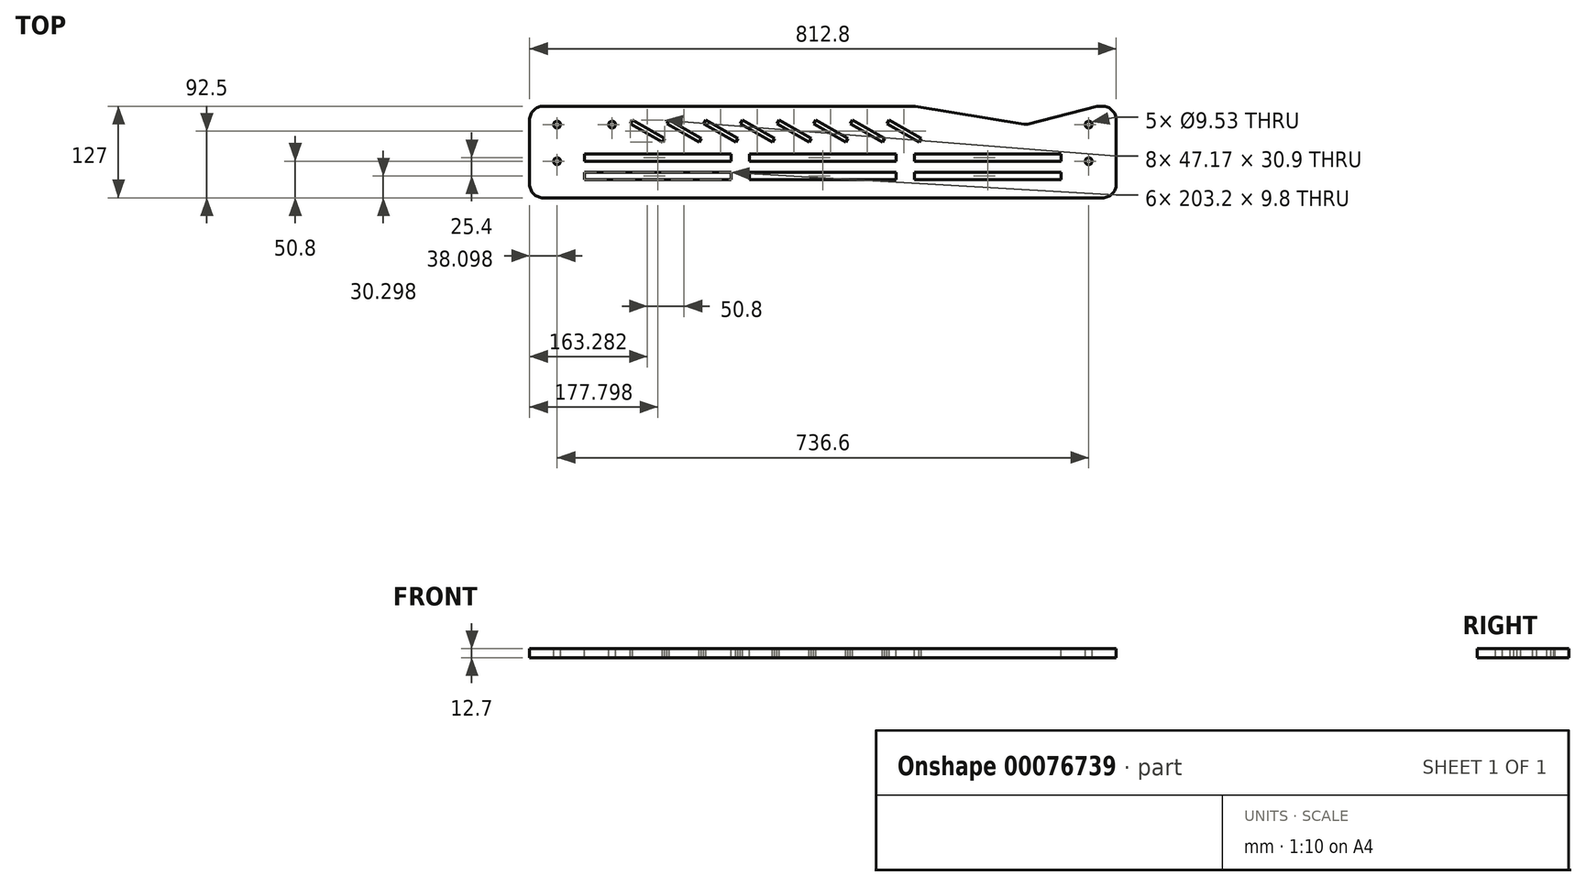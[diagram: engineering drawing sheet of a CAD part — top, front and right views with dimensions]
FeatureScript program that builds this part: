
annotation { "Feature Type Name" : "Feature", "Feature Type Description" : "" }
export const myFeature = defineFeature(function(context is Context, id is Id, definition is map)
    precondition{}
    {
        {
            var Q0;
            Q0=qCreatedBy(makeId("Top.planeOp"),FACE);
            var sketch = newSketch(context, id + "F0", { "sketchPlane" : qUnion([Q0])});
            skLineSegment(sketch, "E0.bottom", {"start": v(-305.25, 25.4) * mm, "end": v(208.06, 25.4) * mm});
            skLineSegment(sketch, "E0.top", {"start": v(-305.25, -101.6) * mm, "end": v(469.45, -101.6) * mm});
            skLineSegment(sketch, "E0.left", {"start": v(-324.3, 6.35) * mm, "end": v(-324.3, -82.55) * mm});
            skLineSegment(sketch, "E0.right", {"start": v(488.5, 6.35) * mm, "end": v(488.5, -82.55) * mm});
            skPoint(sketch, "E1.visualSharp", {"position": v(-324.3, 25.4) * mm});
            skArc(sketch, "E1.filletArc", {"start": v(-305.25, 25.4) * mm, "mid": v(-318.72, 19.82) * mm, "end": v(-324.3, 6.35) * mm});
            skPoint(sketch, "E2.visualSharp", {"position": v(-324.3, -101.6) * mm});
            skArc(sketch, "E2.filletArc", {"start": v(-324.3, -82.55) * mm, "mid": v(-318.72, -96.02) * mm, "end": v(-305.25, -101.6) * mm});
            skPoint(sketch, "E3.visualSharp", {"position": v(488.5, -101.6) * mm});
            skArc(sketch, "E3.filletArc", {"start": v(469.45, -101.6) * mm, "mid": v(482.92, -96.02) * mm, "end": v(488.5, -82.55) * mm});
            skPoint(sketch, "E4.visualSharp", {"position": v(488.5, 25.4) * mm});
            skArc(sketch, "E4.filletArc", {"start": v(488.5, 6.35) * mm, "mid": v(482.92, 19.82) * mm, "end": v(469.45, 25.4) * mm});
            skLineSegment(sketch, "E5.trimOffspring", {"start": v(464.68, 25.4) * mm, "end": v(469.45, 25.4) * mm});
            skLineSegment(sketch, "E6", {"start": v(461.56, 25) * mm, "end": v(365.62, 0.65) * mm});
            skLineSegment(sketch, "E7", {"start": v(360.43, 0.43) * mm, "end": v(210.12, 25.23) * mm});
            skPoint(sketch, "E8.visualSharp", {"position": v(363.04, 0) * mm});
            skArc(sketch, "E8.filletArc", {"start": v(360.43, 0.43) * mm, "mid": v(363.03, 0.27) * mm, "end": v(365.62, 0.65) * mm});
            skPoint(sketch, "E9.visualSharp", {"position": v(209.1, 25.4) * mm});
            skArc(sketch, "E9.filletArc", {"start": v(210.12, 25.23) * mm, "mid": v(209.1, 25.36) * mm, "end": v(208.06, 25.4) * mm});
            skPoint(sketch, "E10.visualSharp", {"position": v(463.1, 25.4) * mm});
            skArc(sketch, "E10.filletArc", {"start": v(464.68, 25.4) * mm, "mid": v(463.1, 25.3) * mm, "end": v(461.56, 25) * mm});
            skSolve(sketch);
        }
        {
            var Q0;
            Q0=makeQuery(id+"F0.imprint","IMPRINT",FACE,{"disambiguationData":[TD([[makeQuery(id+"F0.imprint","IMPRINT",EDGE,{"derivedFrom":sQuery(id+"F0.wireOp",EDGE,"E0.bottom")}),-1.0]])]});
            extrude(context, id + "F1", {"entities" : qUnion([Q0]), "depth" : 12.7 * mm});
        }
        {
            var Q0;
            Q0=makeQuery(id+"F1.opExtrude","CAP_FACE",FACE,{"disambiguationData":[OSD([sQuery(id+"F0.wireOp",EDGE,"E0.bottom"),sQuery(id+"F0.wireOp",EDGE,"E0.top"),sQuery(id+"F0.wireOp",EDGE,"E0.left"),sQuery(id+"F0.wireOp",EDGE,"E0.right"),sQuery(id+"F0.wireOp",EDGE,"965c0fb1-0d6b-43e8-9724-7c81c577700a"),sQuery(id+"F0.wireOp",EDGE,"E1.filletArc"),sQuery(id+"F0.wireOp",EDGE,"E2.filletArc"),sQuery(id+"F0.wireOp",EDGE,"E3.filletArc"),sQuery(id+"F0.wireOp",EDGE,"E4.filletArc"),sQuery(id+"F0.wireOp",EDGE,"E5.trimOffspring")])],"isStart":false});
            var sketch = newSketch(context, id + "F2", { "sketchPlane" : qUnion([Q0])});
            skCircle(sketch, "E11", {"center": v(-286.2, 0) * mm, "radius": 4.76 * mm});
            skCircle(sketch, "E12", {"center": v(-286.2, -50.8) * mm, "radius": 4.76 * mm});
            skCircle(sketch, "E13", {"center": v(450.4, 0) * mm, "radius": 4.76 * mm});
            skCircle(sketch, "E14", {"center": v(450.4, -50.8) * mm, "radius": 4.76 * mm});
            skCircle(sketch, "E15", {"center": v(-210, 0) * mm, "radius": 4.76 * mm});
            skSolve(sketch);
        }
        {
            var Q0;
            Q0=makeQuery(id+"F2.imprint","IMPRINT",FACE,{"disambiguationData":[TD([[makeQuery(id+"F2.imprint","IMPRINT",EDGE,{"derivedFrom":sQuery(id+"F2.wireOp",EDGE,"E11")}),1.0]])]});
            var Q1;
            Q1=makeQuery(id+"F2.imprint","IMPRINT",FACE,{"disambiguationData":[TD([[makeQuery(id+"F2.imprint","IMPRINT",EDGE,{"derivedFrom":sQuery(id+"F2.wireOp",EDGE,"E12")}),1.0]])]});
            var Q2;
            Q2=makeQuery(id+"F2.imprint","IMPRINT",FACE,{"disambiguationData":[TD([[makeQuery(id+"F2.imprint","IMPRINT",EDGE,{"derivedFrom":sQuery(id+"F2.wireOp",EDGE,"E15")}),1.0]])]});
            var Q3;
            Q3=makeQuery(id+"F2.imprint","IMPRINT",FACE,{"disambiguationData":[TD([[makeQuery(id+"F2.imprint","IMPRINT",EDGE,{"derivedFrom":sQuery(id+"F2.wireOp",EDGE,"E13")}),1.0]])]});
            var Q4;
            Q4=makeQuery(id+"F2.imprint","IMPRINT",FACE,{"disambiguationData":[TD([[makeQuery(id+"F2.imprint","IMPRINT",EDGE,{"derivedFrom":sQuery(id+"F2.wireOp",EDGE,"E14")}),1.0]])]});
            extrude(context, id + "F3", {"entities" : qUnion([Q0, Q1, Q2, Q3, Q4]), "operationType" : NewBodyOperationType.REMOVE, "endBound" : BoundingType.THROUGH_ALL, "oppositeDirection" : true, "depth" : 25.4 * mm});
        }
        {
            var Q0;
            Q0=makeQuery(id+"F1.opExtrude","CAP_FACE",FACE,{"disambiguationData":[OSD([sQuery(id+"F0.wireOp",EDGE,"E0.bottom"),sQuery(id+"F0.wireOp",EDGE,"E0.top"),sQuery(id+"F0.wireOp",EDGE,"E0.left"),sQuery(id+"F0.wireOp",EDGE,"E0.right"),sQuery(id+"F0.wireOp",EDGE,"965c0fb1-0d6b-43e8-9724-7c81c577700a"),sQuery(id+"F0.wireOp",EDGE,"E1.filletArc"),sQuery(id+"F0.wireOp",EDGE,"E2.filletArc"),sQuery(id+"F0.wireOp",EDGE,"E3.filletArc"),sQuery(id+"F0.wireOp",EDGE,"E4.filletArc"),sQuery(id+"F0.wireOp",EDGE,"E5.trimOffspring")])],"isStart":false});
            var sketch = newSketch(context, id + "F4", { "sketchPlane" : qUnion([Q0])});
            skLineSegment(sketch, "E16.bottom", {"start": v(412.3, -76.2) * mm, "end": v(209.1, -76.2) * mm});
            skLineSegment(sketch, "E16.top", {"start": v(412.3, -66.4) * mm, "end": v(209.1, -66.4) * mm});
            skLineSegment(sketch, "E16.left", {"start": v(412.3, -76.2) * mm, "end": v(412.3, -66.4) * mm});
            skLineSegment(sketch, "E16.right", {"start": v(209.1, -76.2) * mm, "end": v(209.1, -66.4) * mm});
            skLineSegment(sketch, "E17.0.1.0", {"start": v(412.3, -41) * mm, "end": v(209.1, -41) * mm});
            skLineSegment(sketch, "E17.0.1.1", {"start": v(412.3, -50.8) * mm, "end": v(412.3, -41) * mm});
            skLineSegment(sketch, "E17.0.1.2", {"start": v(412.3, -50.8) * mm, "end": v(209.1, -50.8) * mm});
            skLineSegment(sketch, "E17.0.1.3", {"start": v(209.1, -50.8) * mm, "end": v(209.1, -41) * mm});
            skLineSegment(sketch, "E17.1.0.0", {"start": v(183.7, -66.4) * mm, "end": v(-19.5, -66.4) * mm});
            skLineSegment(sketch, "E17.1.0.1", {"start": v(183.7, -76.2) * mm, "end": v(183.7, -66.4) * mm});
            skLineSegment(sketch, "E17.1.0.2", {"start": v(183.7, -76.2) * mm, "end": v(-19.5, -76.2) * mm});
            skLineSegment(sketch, "E17.1.0.3", {"start": v(-19.5, -76.2) * mm, "end": v(-19.5, -66.4) * mm});
            skLineSegment(sketch, "E17.1.1.0", {"start": v(183.7, -41) * mm, "end": v(-19.5, -41) * mm});
            skLineSegment(sketch, "E17.1.1.1", {"start": v(183.7, -50.8) * mm, "end": v(183.7, -41) * mm});
            skLineSegment(sketch, "E17.1.1.2", {"start": v(183.7, -50.8) * mm, "end": v(-19.5, -50.8) * mm});
            skLineSegment(sketch, "E17.1.1.3", {"start": v(-19.5, -50.8) * mm, "end": v(-19.5, -41) * mm});
            skLineSegment(sketch, "E17.2.0.0", {"start": v(-44.9, -66.4) * mm, "end": v(-248.1, -66.4) * mm});
            skLineSegment(sketch, "E17.2.0.1", {"start": v(-44.9, -76.2) * mm, "end": v(-44.9, -66.4) * mm});
            skLineSegment(sketch, "E17.2.0.2", {"start": v(-44.9, -76.2) * mm, "end": v(-248.1, -76.2) * mm});
            skLineSegment(sketch, "E17.2.0.3", {"start": v(-248.1, -76.2) * mm, "end": v(-248.1, -66.4) * mm});
            skLineSegment(sketch, "E17.2.1.0", {"start": v(-44.9, -41) * mm, "end": v(-248.1, -41) * mm});
            skLineSegment(sketch, "E17.2.1.1", {"start": v(-44.9, -50.8) * mm, "end": v(-44.9, -41) * mm});
            skLineSegment(sketch, "E17.2.1.2", {"start": v(-44.9, -50.8) * mm, "end": v(-248.1, -50.8) * mm});
            skLineSegment(sketch, "E17.2.1.3", {"start": v(-248.1, -50.8) * mm, "end": v(-248.1, -41) * mm});
            skLineSegment(sketch, "E17.direction1", {"start": v(209.1, -76.2) * mm, "end": v(-19.5, -76.2) * mm, "construction": true});
            skLineSegment(sketch, "E17.direction2", {"start": v(209.1, -76.2) * mm, "end": v(209.1, -50.8) * mm, "construction": true});
            skSolve(sketch);
        }
        {
            var Q0;
            Q0=makeQuery(id+"F4.imprint","IMPRINT",FACE,{"disambiguationData":[TD([[makeQuery(id+"F4.imprint","IMPRINT",EDGE,{"derivedFrom":sQuery(id+"F4.wireOp",EDGE,"E16.bottom")}),-1.0]])]});
            var Q1;
            Q1=makeQuery(id+"F4.imprint","IMPRINT",FACE,{"disambiguationData":[TD([[makeQuery(id+"F4.imprint","IMPRINT",EDGE,{"derivedFrom":sQuery(id+"F4.wireOp",EDGE,"E17.0.1.0")}),1.0]])]});
            var Q2;
            Q2=makeQuery(id+"F4.imprint","IMPRINT",FACE,{"disambiguationData":[TD([[makeQuery(id+"F4.imprint","IMPRINT",EDGE,{"derivedFrom":sQuery(id+"F4.wireOp",EDGE,"E17.1.1.0")}),1.0]])]});
            var Q3;
            Q3=makeQuery(id+"F4.imprint","IMPRINT",FACE,{"disambiguationData":[TD([[makeQuery(id+"F4.imprint","IMPRINT",EDGE,{"derivedFrom":sQuery(id+"F4.wireOp",EDGE,"E17.1.0.0")}),1.0]])]});
            var Q4;
            Q4=makeQuery(id+"F4.imprint","IMPRINT",FACE,{"disambiguationData":[TD([[makeQuery(id+"F4.imprint","IMPRINT",EDGE,{"derivedFrom":sQuery(id+"F4.wireOp",EDGE,"E17.2.0.0")}),1.0]])]});
            var Q5;
            Q5=makeQuery(id+"F4.imprint","IMPRINT",FACE,{"disambiguationData":[TD([[makeQuery(id+"F4.imprint","IMPRINT",EDGE,{"derivedFrom":sQuery(id+"F4.wireOp",EDGE,"E17.2.1.0")}),1.0]])]});
            extrude(context, id + "F5", {"entities" : qUnion([Q0, Q1, Q2, Q3, Q4, Q5]), "operationType" : NewBodyOperationType.REMOVE, "endBound" : BoundingType.THROUGH_ALL, "oppositeDirection" : true, "depth" : 25.4 * mm});
        }
        {
            var Q0;
            Q0=makeQuery(id+"F1.opExtrude","CAP_FACE",FACE,{"disambiguationData":[OSD([sQuery(id+"F0.wireOp",EDGE,"E0.bottom"),sQuery(id+"F0.wireOp",EDGE,"E0.top"),sQuery(id+"F0.wireOp",EDGE,"E0.left"),sQuery(id+"F0.wireOp",EDGE,"E0.right"),sQuery(id+"F0.wireOp",EDGE,"965c0fb1-0d6b-43e8-9724-7c81c577700a"),sQuery(id+"F0.wireOp",EDGE,"E1.filletArc"),sQuery(id+"F0.wireOp",EDGE,"E2.filletArc"),sQuery(id+"F0.wireOp",EDGE,"E3.filletArc"),sQuery(id+"F0.wireOp",EDGE,"E4.filletArc"),sQuery(id+"F0.wireOp",EDGE,"E5.trimOffspring")])],"isStart":false});
            var sketch = newSketch(context, id + "F6", { "sketchPlane" : qUnion([Q0])});
            skLineSegment(sketch, "E18.bottom", {"start": v(-181.43, 6.35) * mm, "end": v(-137.43, -19.05) * mm});
            skLineSegment(sketch, "E18.top", {"start": v(-184.6, 0.85) * mm, "end": v(-140.6, -24.55) * mm});
            skLineSegment(sketch, "E18.left", {"start": v(-181.43, 6.35) * mm, "end": v(-184.6, 0.85) * mm});
            skLineSegment(sketch, "E18.right", {"start": v(-137.43, -19.05) * mm, "end": v(-140.6, -24.55) * mm});
            skLineSegment(sketch, "E19.1.0.0", {"start": v(-130.63, 6.35) * mm, "end": v(-86.63, -19.05) * mm});
            skLineSegment(sketch, "E19.1.0.1", {"start": v(-133.8, 0.85) * mm, "end": v(-89.8, -24.55) * mm});
            skLineSegment(sketch, "E19.1.0.2", {"start": v(-130.63, 6.35) * mm, "end": v(-133.8, 0.85) * mm});
            skLineSegment(sketch, "E19.1.0.3", {"start": v(-86.63, -19.05) * mm, "end": v(-89.8, -24.55) * mm});
            skLineSegment(sketch, "E19.2.0.0", {"start": v(-79.83, 6.35) * mm, "end": v(-35.83, -19.05) * mm});
            skLineSegment(sketch, "E19.2.0.1", {"start": v(-83, 0.85) * mm, "end": v(-39, -24.55) * mm});
            skLineSegment(sketch, "E19.2.0.2", {"start": v(-79.83, 6.35) * mm, "end": v(-83, 0.85) * mm});
            skLineSegment(sketch, "E19.2.0.3", {"start": v(-35.83, -19.05) * mm, "end": v(-39, -24.55) * mm});
            skLineSegment(sketch, "E19.3.0.0", {"start": v(-29.03, 6.35) * mm, "end": v(14.97, -19.05) * mm});
            skLineSegment(sketch, "E19.3.0.1", {"start": v(-32.2, 0.85) * mm, "end": v(11.8, -24.55) * mm});
            skLineSegment(sketch, "E19.3.0.2", {"start": v(-29.03, 6.35) * mm, "end": v(-32.2, 0.85) * mm});
            skLineSegment(sketch, "E19.3.0.3", {"start": v(14.97, -19.05) * mm, "end": v(11.8, -24.55) * mm});
            skLineSegment(sketch, "E19.4.0.0", {"start": v(21.77, 6.35) * mm, "end": v(65.77, -19.05) * mm});
            skLineSegment(sketch, "E19.4.0.1", {"start": v(18.6, 0.85) * mm, "end": v(62.6, -24.55) * mm});
            skLineSegment(sketch, "E19.4.0.2", {"start": v(21.77, 6.35) * mm, "end": v(18.6, 0.85) * mm});
            skLineSegment(sketch, "E19.4.0.3", {"start": v(65.77, -19.05) * mm, "end": v(62.6, -24.55) * mm});
            skLineSegment(sketch, "E19.5.0.0", {"start": v(72.57, 6.35) * mm, "end": v(116.57, -19.05) * mm});
            skLineSegment(sketch, "E19.5.0.1", {"start": v(69.4, 0.85) * mm, "end": v(113.4, -24.55) * mm});
            skLineSegment(sketch, "E19.5.0.2", {"start": v(72.57, 6.35) * mm, "end": v(69.4, 0.85) * mm});
            skLineSegment(sketch, "E19.5.0.3", {"start": v(116.57, -19.05) * mm, "end": v(113.4, -24.55) * mm});
            skLineSegment(sketch, "E19.6.0.0", {"start": v(123.37, 6.35) * mm, "end": v(167.37, -19.05) * mm});
            skLineSegment(sketch, "E19.6.0.1", {"start": v(120.2, 0.85) * mm, "end": v(164.2, -24.55) * mm});
            skLineSegment(sketch, "E19.6.0.2", {"start": v(123.37, 6.35) * mm, "end": v(120.2, 0.85) * mm});
            skLineSegment(sketch, "E19.6.0.3", {"start": v(167.37, -19.05) * mm, "end": v(164.2, -24.55) * mm});
            skLineSegment(sketch, "E19.7.0.0", {"start": v(174.17, 6.35) * mm, "end": v(218.17, -19.05) * mm});
            skLineSegment(sketch, "E19.7.0.1", {"start": v(171, 0.85) * mm, "end": v(215, -24.55) * mm});
            skLineSegment(sketch, "E19.7.0.2", {"start": v(174.17, 6.35) * mm, "end": v(171, 0.85) * mm});
            skLineSegment(sketch, "E19.7.0.3", {"start": v(218.17, -19.05) * mm, "end": v(215, -24.55) * mm});
            skLineSegment(sketch, "E19.direction1", {"start": v(-184.6, 0.85) * mm, "end": v(-133.8, 0.85) * mm, "construction": true});
            skSolve(sketch);
        }
        {
            var Q0;
            Q0=makeQuery(id+"F6.imprint","IMPRINT",FACE,{"disambiguationData":[TD([[makeQuery(id+"F6.imprint","IMPRINT",EDGE,{"derivedFrom":sQuery(id+"F6.wireOp",EDGE,"E18.bottom")}),-1.0]])]});
            var Q1;
            Q1=makeQuery(id+"F6.imprint","IMPRINT",FACE,{"disambiguationData":[TD([[makeQuery(id+"F6.imprint","IMPRINT",EDGE,{"derivedFrom":sQuery(id+"F6.wireOp",EDGE,"E19.1.0.0")}),-1.0]])]});
            var Q2;
            Q2=makeQuery(id+"F6.imprint","IMPRINT",FACE,{"disambiguationData":[TD([[makeQuery(id+"F6.imprint","IMPRINT",EDGE,{"derivedFrom":sQuery(id+"F6.wireOp",EDGE,"E19.2.0.0")}),-1.0]])]});
            var Q3;
            Q3=makeQuery(id+"F6.imprint","IMPRINT",FACE,{"disambiguationData":[TD([[makeQuery(id+"F6.imprint","IMPRINT",EDGE,{"derivedFrom":sQuery(id+"F6.wireOp",EDGE,"E19.3.0.0")}),-1.0]])]});
            var Q4;
            Q4=makeQuery(id+"F6.imprint","IMPRINT",FACE,{"disambiguationData":[TD([[makeQuery(id+"F6.imprint","IMPRINT",EDGE,{"derivedFrom":sQuery(id+"F6.wireOp",EDGE,"E19.4.0.0")}),-1.0]])]});
            var Q5;
            Q5=makeQuery(id+"F6.imprint","IMPRINT",FACE,{"disambiguationData":[TD([[makeQuery(id+"F6.imprint","IMPRINT",EDGE,{"derivedFrom":sQuery(id+"F6.wireOp",EDGE,"E19.5.0.0")}),-1.0]])]});
            var Q6;
            Q6=makeQuery(id+"F6.imprint","IMPRINT",FACE,{"disambiguationData":[TD([[makeQuery(id+"F6.imprint","IMPRINT",EDGE,{"derivedFrom":sQuery(id+"F6.wireOp",EDGE,"E19.6.0.0")}),-1.0]])]});
            var Q7;
            Q7=makeQuery(id+"F6.imprint","IMPRINT",FACE,{"disambiguationData":[TD([[makeQuery(id+"F6.imprint","IMPRINT",EDGE,{"derivedFrom":sQuery(id+"F6.wireOp",EDGE,"E19.7.0.0")}),-1.0]])]});
            extrude(context, id + "F7", {"entities" : qUnion([Q0, Q1, Q2, Q3, Q4, Q5, Q6, Q7]), "operationType" : NewBodyOperationType.REMOVE, "endBound" : BoundingType.THROUGH_ALL, "oppositeDirection" : true, "depth" : 25.4 * mm});
        }
    });
